# Revit family: 05-9757-CA-CL
name_source: partatom
category: Luminarias
revit_build: Autodesk Revit 2017 (Build: 20160225_1515(x64)
units: mm (PartAtom-declared; Revit-internal decimal feet)

## family parameters
Anfitrión = Cara
Compartido = Sí
Corte con vacíos al cargar = No
Cota de conector redondo = Diámetro de uso
Número OmniClass = 23.80.70.00
Origen de luz = No
Punto de cálculo de habitación = No
Tipo de pieza = Normal
Título OmniClass = Lighting

## types (1)
- 05-9757-CA-CL
    Acabado = Pulido, Transparente
    CRI = 80
    Carga aparente = 0 VA
    Catálogo = Outdoor
    CodigoGubimclass = 50.60.50.20
    CodigoOmniclass = 21-04 50 40
    CodigoUniclass2015 = EF_70_80
    CodigoUniformat2010 = D5040
    DescripcionGubimclass = Iluminación interior
    DescripcionOmniclass = Lighting
    DescripcionUniclass2015 = Lighting
    DescripcionUniformat2010 = Lighting
    EAN13 = 8435381438340
    Eficiencia energética = LED A++
    Elevación por defecto = 1000 mm  [stored 3.28084 ft]
    Etiqueta V/f = 100-240V/50-60Hz
    Fabricante = LEDS C4
    Familia = Gea Effect Round
    FechaVersion = Julio 2020
    Ficha = http://files.leds-c4.com
    Fotometría = http://files.leds-c4.com
    Fuente de luz = 1xLED 2.2 162.00 lm
    IK = IK10
    IMC = http://files.leds-c4.com
    IP = IP65
    IfcExportAs = IfcLightFixture
IfcLightFixture
    IfcExportType = NOTDEFINED
    Imagen web = http://files.leds-c4.com
    LDT = http://files.leds-c4.com
    Lumenes reales (lm) = 62
    Material = Acero inoxidable AISI 316, Cristal
    Peso neto (KG) = 0.35
    Pluma comercial = http://files.leds-c4.com
    Producto descatalogado = Catalogado ES
    Rayo de luz = Check Photometric file
    Referencia = 05-9757-CA-CL
    Temperatura color led (K) = Blanco cálido - 3000K
    Tender text (Castellano) = LEDS C4
Gea Effect Round
05-9757-CA-CL

Empotrado de pared de uso exterior para iluminar frontalmente y hacia abajo. 

Incluye caja de empotrar. Especialmente diseñada para ocultar toda la tornillería. Apto para instalar en ambientes con atmósfera marina. Material estructura: Acero inoxidable AISI 316. Acabado estructura: Pulido. Material difusor: Cristal. Acabado difusor: Transparente. Protección contra los rayos ultravioleta. Garantía: 5 Años.

Peso neto del producto (Kg): 0.350
Anchura o diámetro del producto (mm): 95
Salida del producto (mm): 72
Ø del agujero para empotrar (mm): 80

Clase 1. Prueba hilo incandescente: 850. IP: IP65. IK: IK10. LED. Nº de portalámparas o Leds: 1. Marca del LED: CREE. Marca del Driver: HILITE. Potencia máxima de la fuente de luz: 2.2W. Temperatura de color: Blanco cálido - 3000K. Índice de reproducción cromática: 80. Steps Mac Adam: 3. Diámetro máximo de la bombilla que admite la luminaria: 50.000h L80B20. UGR:  12.3. Riesgo fotobiológico: RG2. Flujo real (lm): 62. Flujo nominal (lm): 162. Lm/W reales: 17. Rango de voltaje/frecuencia: 100-240 VAC. Voltaje: 3. Equipo incluido: Si, electrónico. Equipo multivoltaje incluido. Potencia total: 3.7. Factor de potencia: 0.56.
    Tender text (English) = LEDS C4
Gea Effect Round
05-9757-CA-CL

Wall recessed for outdoor use. 

For frontal lighting and downlighting. Includes flush-mounting box. Specially designed to conceal all mounting screws. Suitable for installation in marine environments. Structure material: Stainless steel AISI316. Structure finish: Polished. Diffuser material: Glass. Diffuser finish: Transparent. UV protection. Warranty: 5 Years.

Product net weight (Kg): 0.350
Product width or diameter (mm): 95
Product aperture (mm): 72
Ø of the hole for recessing (mm): 80

Class 1. Glow wire test: 850. IP: IP65. IK: IK10. LED. No. of lampholders or LEDs: 1. LED brand: CREE. Driver brand: HILITE. Maximum power of light source: 2.2W. Colour temperature: LED warm-white 3000K. Colour rendering index: 80. MacAdam Steps: 3. Maximum diameter of luminaire bulb: 50.000h L80B20. UGR:  12.3. Photobiological risk: RG2. Real flux (lm): 62. Nominal flux (lm): 162. Lm/Real W: 17. Voltage and frequency range: 100-240 VAC. Voltage: 3. Gear included: Yes, electronic. Multi-voltage gear included. Total power: 3.7. Power factor: 0.56.
    Tipo = Empotrable de pared
    Vatios (W) = 3.7
    Versión = v1

note: [stored X ft] marks values corroborated as IEEE doubles in the binary element streams (Revit-internal decimal feet)
